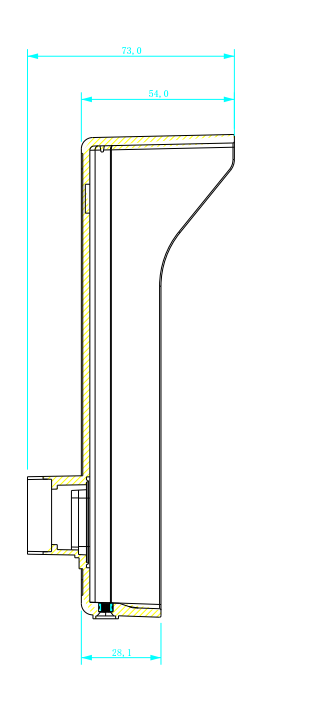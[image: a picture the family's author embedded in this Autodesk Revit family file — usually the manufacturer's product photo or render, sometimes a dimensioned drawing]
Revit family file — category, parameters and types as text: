
# Revit family: SP-03
name_source: partatom
category: Устройства связи
units: mm (PartAtom-declared; Revit-internal decimal feet)

## family parameters
Всегда вертикально = Нет
На основе рабочей плоскости = Да
Общий = Да
При загрузке вырезать с полостями = Нет
Размер круглого соединителя = Использовать диаметр
Сохранять ориентацию аннотаций = Нет
Тип детали = Нормальный
Точка принадлежности помещению = Нет

## types (1)
- SP-03
    ADSK_URL документации изделия = https://wiki.bas-ip.com
    ADSK_URL страницы изделия = https://www.bas-ip.ru
    ADSK_Версия Revit = Revit 2020
    ADSK_Единица измерения = шт
    ADSK_Завод-изготовитель = BAS-IP
    ADSK_Классификация нагрузок = Абонентское аудиоустройство
    ADSK_Количество фаз = 1
    ADSK_Коэффициент мощности = 0.9
    ADSK_Марка = SP-03
    ADSK_Наименование = Абонентское аудиоустройство SP-03
    ADSK_Наименование краткое = SP-03
    ADSK_Напряжение = 12 В
    ADSK_Номинальная мощность = 6 Вт
    ADSK_Полная мощность = 6 В·А
    ADSK_Размер_Длина = 184 мм
    ADSK_Размер_Толщина = 28 мм
    ADSK_Размер_Ширина = 106 мм
    BIM library = https://bimlib.ru
    URL = https://www.bas-ip.ru
    Вызов лифта = Есть
    Вызов на монитор консьержа = Есть
    Габаритные размеры = 184×106×28 мм
    Группа модели = Абонентское аудиоустройство SP-03
    Дополнительная функция = Подключение дверного звонка
    Изготовитель = BAS-IP
    Изображение типоразмера = <Нет>
    Количество клавиш управления = 6
    Количество поддерживаемых учетных записей VoIP = 1
    Количество уровней громкости = 6
    Корпус = Пластик
    Материал корпуса = Материал белый
    Метод приемо-передачи аудиосигнала = Full Duplex
    Метод установки = Настенная
    Описание = Абонентское аудиоустройство SP-03 - Абонентское IP аудио устройство с поддержкой SIP, P2P и внутреннего протокола BAS-IP
    Открытие замка вызываемой панели = Есть
    Отметка по умолчанию = 0 мм
    Переадресация звонка = Есть
    Питание = PoE, +12 В (+11% -6%)
    Поддержка внутреннего протокола BAS-IP = Есть
    Поддержка протокола SIP 2.0 = Есть
    Подключение к сети = 1 PoE порт IEEE 802.3af
    Режим "Без звука" = Есть
    Режим "Не беспокоить" = Есть
    Способ настройки и программирования = WEB-интерфейс
    Тип поддерживаемого протокола = IPv4
    Тип поддерживаемых кодеков = G.711μ/A
    Трехцветный световой индикатор = Есть
    Цветовое решение = Белый, черный
